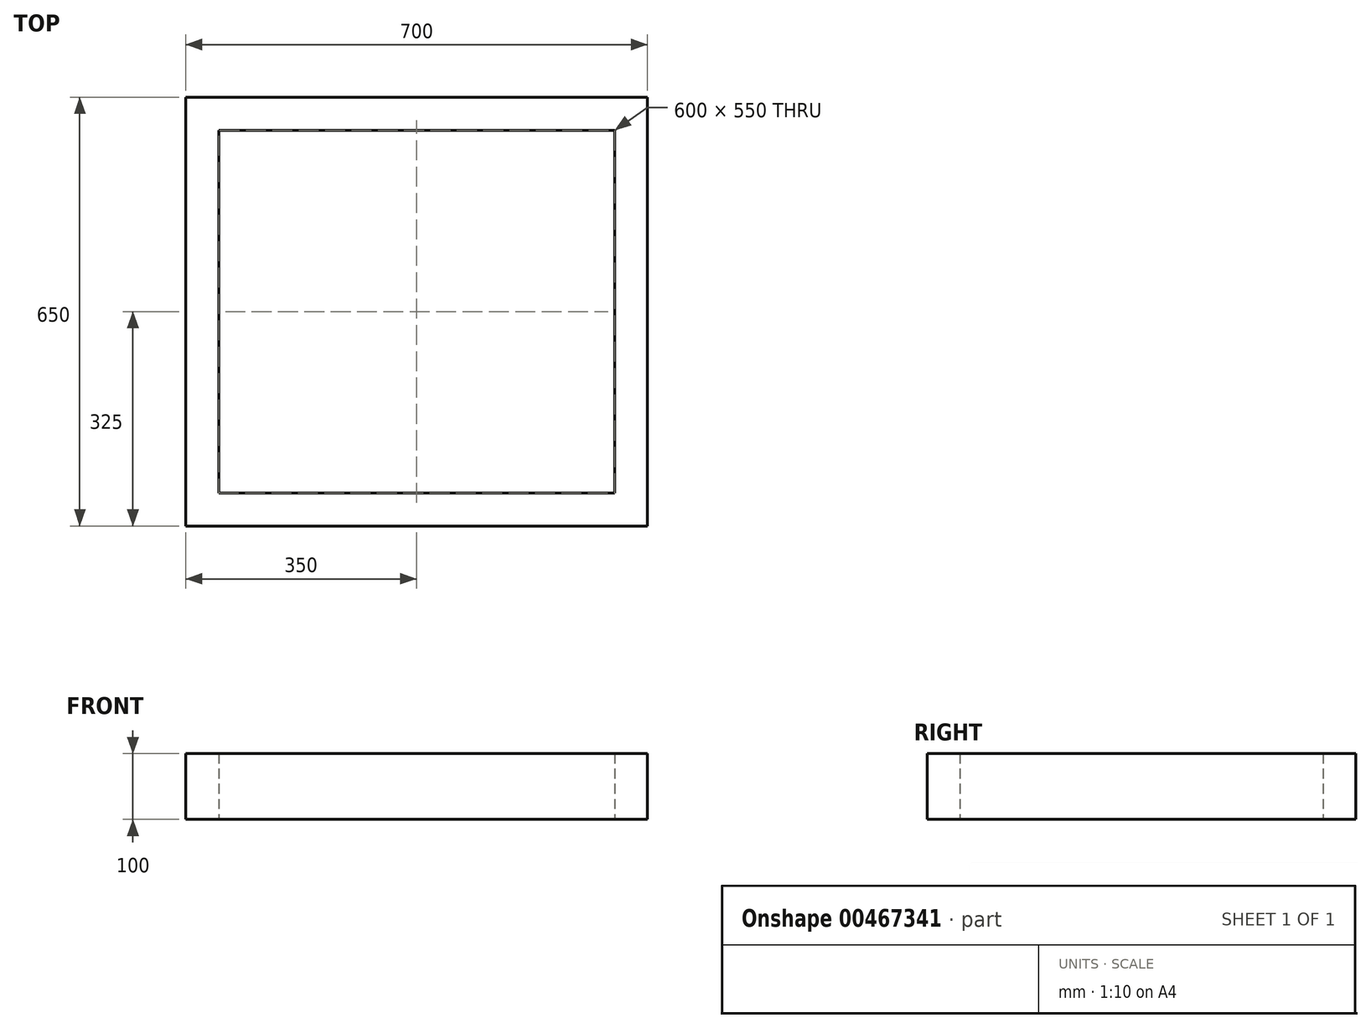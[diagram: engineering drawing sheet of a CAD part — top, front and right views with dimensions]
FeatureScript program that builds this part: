
annotation { "Feature Type Name" : "Feature", "Feature Type Description" : "" }
export const myFeature = defineFeature(function(context is Context, id is Id, definition is map)
    precondition{}
    {
        {
            var Q0;
            Q0=qCreatedBy(makeId("Top.planeOp"),FACE);
            var sketch = newSketch(context, id + "F0", { "sketchPlane" : qUnion([Q0])});
            skLineSegment(sketch, "E0.bottom", {"start": v(350, -325) * mm, "end": v(-350, -325) * mm});
            skLineSegment(sketch, "E0.top", {"start": v(350, 325) * mm, "end": v(-350, 325) * mm});
            skLineSegment(sketch, "E0.left", {"start": v(350, -325) * mm, "end": v(350, 325) * mm});
            skLineSegment(sketch, "E0.right", {"start": v(-350, -325) * mm, "end": v(-350, 325) * mm});
            skPoint(sketch, "E0.middle", {"position": v(0, 0) * mm});
            skLineSegment(sketch, "E1.bottom", {"start": v(300, -275) * mm, "end": v(-300, -275) * mm});
            skLineSegment(sketch, "E1.top", {"start": v(300, 275) * mm, "end": v(-300, 275) * mm});
            skLineSegment(sketch, "E1.left", {"start": v(300, -275) * mm, "end": v(300, 275) * mm});
            skLineSegment(sketch, "E1.right", {"start": v(-300, -275) * mm, "end": v(-300, 275) * mm});
            skSolve(sketch);
        }
        {
            var Q0;
            Q0=makeQuery(id+"F0.imprint","IMPRINT",FACE,{"disambiguationData":[TD([[makeQuery(id+"F0.imprint","IMPRINT",EDGE,{"derivedFrom":sQuery(id+"F0.wireOp",EDGE,"E0.bottom")}),-1.0]])]});
            extrude(context, id + "F1", {"entities" : qUnion([Q0]), "depth" : 100 * mm});
        }
    });
